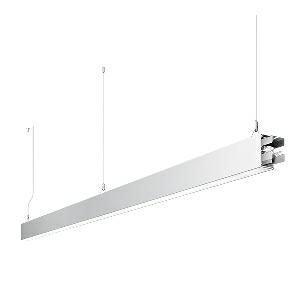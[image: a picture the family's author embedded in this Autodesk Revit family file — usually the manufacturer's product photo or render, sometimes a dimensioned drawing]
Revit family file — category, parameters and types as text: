
# Revit family: dotoo_line_-_dlp_3000_840_d_sta_00805785_3b44
name_source: partatom
category: Lighting Fixtures
units: mm (PartAtom-declared; Revit-internal decimal feet)

## family parameters
Cut with Voids When Loaded = No
Host = Face
Light Source = No
Part Type = Normal
Room Calculation Point = No
Round Connector Dimension = Use Diameter
Shared = No

## types (1)
- DOTOO.line - DLP 3000/840/D STA (1 x LED, 2750 lm, 4000K)
    Apparent Load = 26 VA
    Approval mark = CE
    CIE Flux Codes = 67 91 98 100 100
    Color Rendering = 80-89
    Color Temperature = 4000K
    Control Gear = Electronic ballast
    Default Elevation = 1800 mm
    Description = DLP 3000/840/D|Suspended luminaire|light source: LED|connected load: 220-240 V, 50/60 Hz|Power consumption: approx. 26 W|standby: approx. 0,15|luminous flux: 2750 lm|luminous efficacy: 105 lm/W|light distribution: Direct|direct ratio: approx. 100 %|colour temperature: Cold white, ca. 4000 K|color rendering index (CRI): >= 80|chromaticity tolerance:  3 SDCM|System of protection: IP 40|technology: Continuously dimmable|luminaire body|material: Sectional aluminium|colour: White|lamp cover: Acrylic (PMMA), Clear|mains lead: 2.00 m With free stranded wires|Fastening: Steel cable 0.3 - 0.7 m|glare control: Prism aperture|luminance(L65): <= 3000 cd/m|unified glare rating(4H 8H): <=  19|special features: DALI Load 1x, TouchDIM - dimming via standard switch, Through-wired, up to 18 m on one mains connection, Flicker-free, Suitable as emergency lighting, Start luminaire with mains connection, Mechanical and electrical connection of the individual modules without tools|
    Frequency = 50 Hz
    Height = 110 mm
    Lamp = 1 x LED
    Lamp Light Flux = 2750 lm
    Lamp count = 1
    Length = 2250 mm
    Luminous efficacy = 106 lm/W
    Manufacturer = Waldmann
    ModVariant = No
    Model = 00805785
    Mounting Place = Ceiling
    Mounting Type = Pendant
    Number of Poles = 1
    OnlyDefault = Yes
    Power Factor = 1
    Product Name = DOTOO.line - DLP 3000/840/D STA
    Product group = Suspended luminaire
    ProductGroupID = 9
    Protection Class = Protection class I
    Protection Degree = IP 40
    RLX_Detail_Level = 1
    RLX_Emergency_Light_Flux = 0 lm
    RLX_Emergency_Type = 0
    RLX_Emergency_Type_DB = No
    RlxData = <blob elided: 23109 chars, md5=80096ce1>
    Socket = socket
    Standby Power = 0 W
    System Light Flux = 2750 lm
    System Power = 26 W
    Type Comments = Product without accessories
    Type Image = 113313000-00692603.jpg
    URL = http://relux.com
    VarID = ---
    Voltage = 230 V
    Voltage Range = 220-240 V
    Weight = 0.00 kg
    Width = 60 mm  [stored 0.19685 ft]

note: [stored X ft] marks values corroborated as IEEE doubles in the binary element streams (Revit-internal decimal feet)

## geometry (parser evidence)
native form markers: Blend x4, Sweep x13
no freeform markers — native parametric forms only
